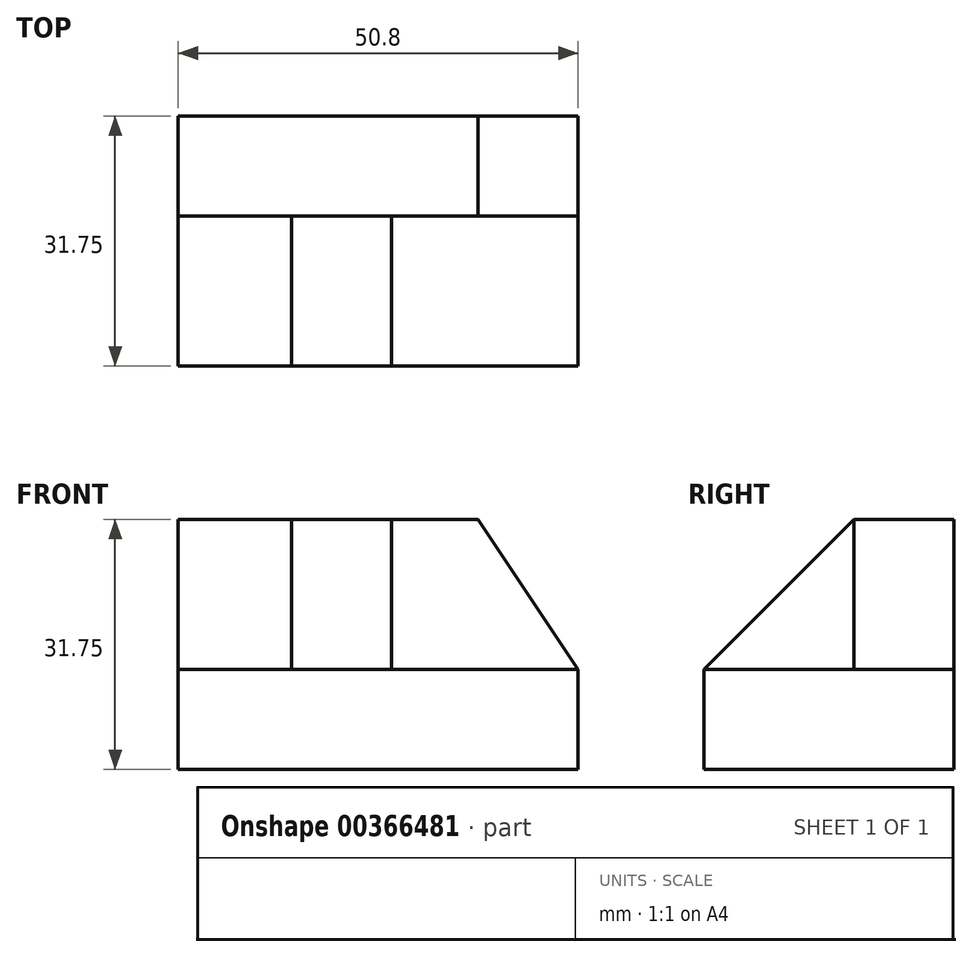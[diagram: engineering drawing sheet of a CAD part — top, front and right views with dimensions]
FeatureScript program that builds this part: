
annotation { "Feature Type Name" : "Feature", "Feature Type Description" : "" }
export const myFeature = defineFeature(function(context is Context, id is Id, definition is map)
    precondition{}
    {
        {
            var Q0;
            Q0=qCreatedBy(makeId("Top.planeOp"),FACE);
            var sketch = newSketch(context, id + "F0", { "sketchPlane" : qUnion([Q0])});
            skLineSegment(sketch, "E0", {"start": v(0, 0) * mm, "end": v(50.8, 0) * mm});
            skLineSegment(sketch, "E1", {"start": v(50.8, 0) * mm, "end": v(50.8, 31.75) * mm});
            skLineSegment(sketch, "E2", {"start": v(50.8, 31.75) * mm, "end": v(0, 31.75) * mm});
            skLineSegment(sketch, "E3", {"start": v(0, 31.75) * mm, "end": v(0, 0) * mm});
            skSolve(sketch);
        }
        {
            var Q0;
            Q0 = qSketchRegion(id + "F0", true);
            extrude(context, id + "F1", {"entities" : qUnion([Q0]), "depth" : 12.7 * mm});
        }
        {
            var Q0;
            Q0=makeQuery(id+"F1.opExtrude","CAP_FACE",FACE,{"disambiguationData":[OSD([sQuery(id+"F0.wireOp",EDGE,"E0"),sQuery(id+"F0.wireOp",EDGE,"E1"),sQuery(id+"F0.wireOp",EDGE,"E2"),sQuery(id+"F0.wireOp",EDGE,"E3")])],"isStart":false});
            var sketch = newSketch(context, id + "F2", { "sketchPlane" : qUnion([Q0])});
            skLineSegment(sketch, "E4", {"start": v(0, 31.75) * mm, "end": v(50.8, 31.75) * mm});
            skLineSegment(sketch, "E5", {"start": v(50.8, 31.75) * mm, "end": v(50.8, 19.05) * mm});
            skLineSegment(sketch, "E6", {"start": v(50.8, 19.05) * mm, "end": v(0, 19.05) * mm});
            skLineSegment(sketch, "E7", {"start": v(0, 19.05) * mm, "end": v(0, 31.75) * mm});
            skSolve(sketch);
        }
        {
            var Q0;
            Q0=makeQuery(id+"F2.imprint","IMPRINT",FACE,{"disambiguationData":[TD([[makeQuery(id+"F2.imprint","IMPRINT",EDGE,{"derivedFrom":sQuery(id+"F2.wireOp",EDGE,"E4")}),1.0]])]});
            extrude(context, id + "F3", {"entities" : qUnion([Q0]), "operationType" : NewBodyOperationType.ADD, "depth" : 19.05 * mm});
        }
        {
            var Q0;
            Q0=makeQuery(id+"F3.opExtrude","SWEPT_FACE",FACE,{"disambiguationData":[OSD([sQuery(id+"F2.wireOp",EDGE,"E6")])]});
            var sketch = newSketch(context, id + "F4", { "sketchPlane" : qUnion([Q0])});
            skLineSegment(sketch, "E8", {"start": v(50.8, 12.7) * mm, "end": v(50.8, 31.75) * mm});
            skLineSegment(sketch, "E9", {"start": v(50.8, 31.75) * mm, "end": v(38.1, 31.75) * mm});
            skLineSegment(sketch, "E10", {"start": v(38.1, 31.75) * mm, "end": v(50.8, 12.7) * mm});
            skSolve(sketch);
        }
        {
            var Q0;
            Q0=makeQuery(id+"F4.imprint","IMPRINT",FACE,{"disambiguationData":[TD([[makeQuery(id+"F4.imprint","IMPRINT",EDGE,{"derivedFrom":sQuery(id+"F4.wireOp",EDGE,"E8")}),-1.0]])]});
            extrude(context, id + "F5", {"entities" : qUnion([Q0]), "operationType" : NewBodyOperationType.REMOVE, "oppositeDirection" : true, "depth" : 12.7 * mm});
        }
        {
            var Q0;
            Q0=makeQuery(id+"F3.opExtrude","SWEPT_FACE",FACE,{"disambiguationData":[OSD([sQuery(id+"F2.wireOp",EDGE,"E6")])]});
            var sketch = newSketch(context, id + "F6", { "sketchPlane" : qUnion([Q0])});
            skLineSegment(sketch, "E11", {"start": v(14.4, 12.7) * mm, "end": v(14.4, 31.75) * mm});
            skLineSegment(sketch, "E12", {"start": v(14.4, 31.75) * mm, "end": v(27.1, 31.75) * mm});
            skLineSegment(sketch, "E13", {"start": v(27.1, 31.75) * mm, "end": v(27.1, 12.7) * mm});
            skLineSegment(sketch, "E14", {"start": v(27.1, 12.7) * mm, "end": v(14.4, 12.7) * mm});
            skSolve(sketch);
        }
        {
            var Q0;
            Q0=makeQuery(id+"F6.imprint","IMPRINT",FACE,{"disambiguationData":[TD([[makeQuery(id+"F6.imprint","IMPRINT",EDGE,{"derivedFrom":sQuery(id+"F6.wireOp",EDGE,"E11")}),-1.0]])]});
            extrude(context, id + "F7", {"entities" : qUnion([Q0]), "operationType" : NewBodyOperationType.ADD, "depth" : 19.05 * mm});
        }
        {
            var Q0;
            Q0=makeQuery(id+"F7.opExtrude","SWEPT_FACE",FACE,{"disambiguationData":[OSD([sQuery(id+"F6.wireOp",EDGE,"E13")])]});
            var sketch = newSketch(context, id + "F8", { "sketchPlane" : qUnion([Q0])});
            skLineSegment(sketch, "E15", {"start": v(19.05, 31.75) * mm, "end": v(0, 12.7) * mm});
            skLineSegment(sketch, "E16", {"start": v(0, 12.7) * mm, "end": v(0, 31.75) * mm});
            skLineSegment(sketch, "E17", {"start": v(0, 31.75) * mm, "end": v(19.05, 31.75) * mm});
            skSolve(sketch);
        }
        {
            var Q0;
            Q0=makeQuery(id+"F8.imprint","IMPRINT",FACE,{"disambiguationData":[TD([[makeQuery(id+"F8.imprint","IMPRINT",EDGE,{"derivedFrom":sQuery(id+"F8.wireOp",EDGE,"E15")}),-1.0]])]});
            extrude(context, id + "F9", {"entities" : qUnion([Q0]), "operationType" : NewBodyOperationType.REMOVE, "oppositeDirection" : true, "depth" : 25.4 * mm});
        }
    });
